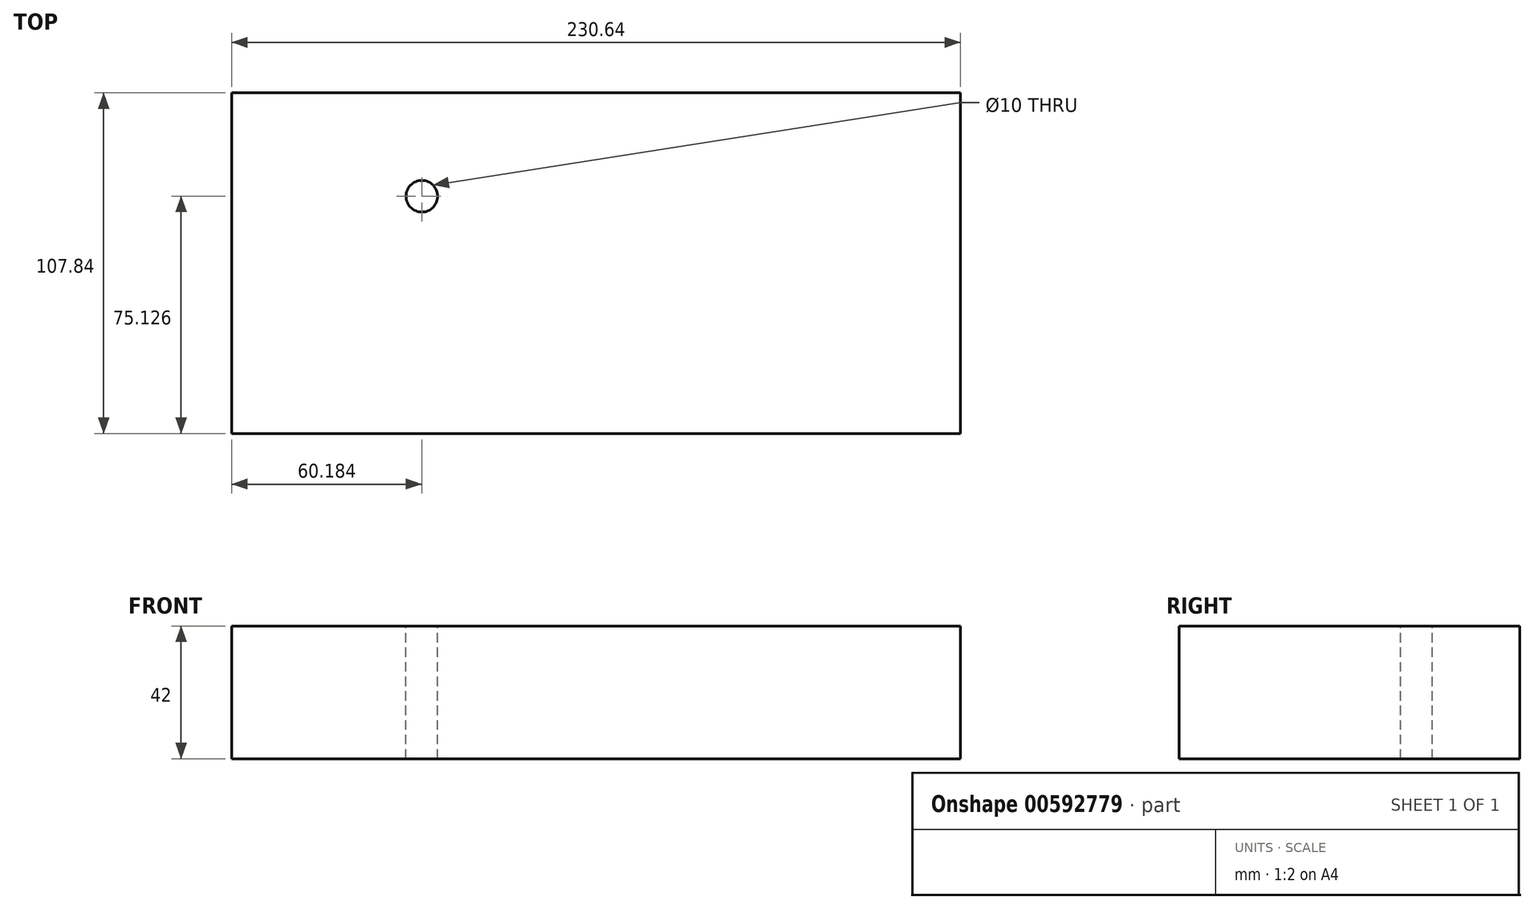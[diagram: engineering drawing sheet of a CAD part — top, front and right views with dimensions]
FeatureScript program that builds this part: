
annotation { "Feature Type Name" : "Feature", "Feature Type Description" : "" }
export const myFeature = defineFeature(function(context is Context, id is Id, definition is map)
    precondition{}
    {
        {
            var Q0;
            Q0=qCreatedBy(makeId("Top.planeOp"),FACE);
            var sketch = newSketch(context, id + "F0", { "sketchPlane" : qUnion([Q0])});
            skLineSegment(sketch, "E0.bottom", {"start": v(-115.32, 53.92) * mm, "end": v(115.32, 53.92) * mm});
            skLineSegment(sketch, "E0.top", {"start": v(-115.32, -53.92) * mm, "end": v(115.32, -53.92) * mm});
            skLineSegment(sketch, "E0.left", {"start": v(-115.32, 53.92) * mm, "end": v(-115.32, -53.92) * mm});
            skLineSegment(sketch, "E0.right", {"start": v(115.32, 53.92) * mm, "end": v(115.32, -53.92) * mm});
            skPoint(sketch, "E0.middle", {"position": v(0, 0) * mm});
            skCircle(sketch, "E1", {"center": v(-55.14, 21.2) * mm, "radius": 5 * mm});
            skSolve(sketch);
        }
        {
            var Q0;
            Q0=makeQuery(id+"F0.imprint","IMPRINT",FACE,{"disambiguationData":[TD([[makeQuery(id+"F0.imprint","IMPRINT",EDGE,{"derivedFrom":sQuery(id+"F0.wireOp",EDGE,"E0.bottom")}),-1.0]])]});
            extrude(context, id + "F1", {"entities" : qUnion([Q0]), "oppositeDirection" : true, "depth" : 42 * mm, "offsetDistance" : 25 * mm});
        }
    });
